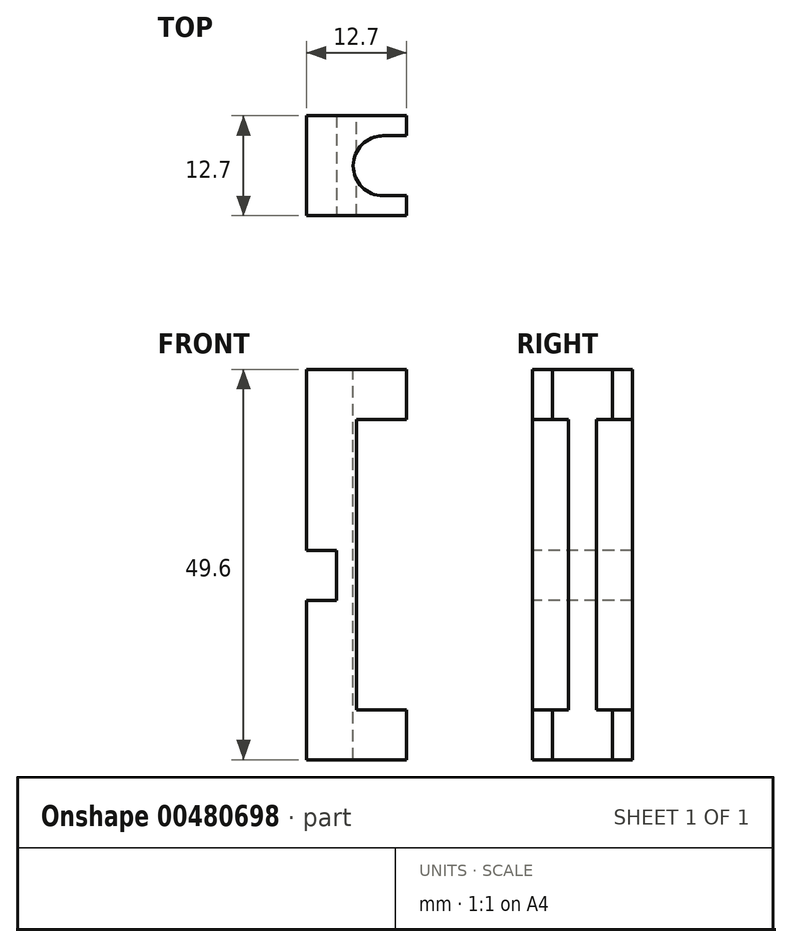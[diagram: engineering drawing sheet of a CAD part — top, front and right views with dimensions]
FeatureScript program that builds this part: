
annotation { "Feature Type Name" : "Feature", "Feature Type Description" : "" }
export const myFeature = defineFeature(function(context is Context, id is Id, definition is map)
    precondition{}
    {
        {
            var Q0;
            Q0=qCreatedBy(makeId("Front.planeOp"),FACE);
            var sketch = newSketch(context, id + "F0", { "sketchPlane" : qUnion([Q0])});
            skLineSegment(sketch, "E0.bottom", {"start": v(-21.97, -16.87) * mm, "end": v(-15.62, -16.87) * mm});
            skLineSegment(sketch, "E0.top", {"start": v(-21.97, 32.73) * mm, "end": v(-15.62, 32.73) * mm});
            skLineSegment(sketch, "E0.left", {"start": v(-21.97, -16.87) * mm, "end": v(-21.97, 32.73) * mm});
            skLineSegment(sketch, "E0.right", {"start": v(-15.62, -16.87) * mm, "end": v(-15.62, 32.73) * mm});
            skLineSegment(sketch, "E1", {"start": v(-15.62, 26.38) * mm, "end": v(-9.27, 26.38) * mm});
            skLineSegment(sketch, "E2", {"start": v(-9.27, 26.38) * mm, "end": v(-9.27, 32.73) * mm});
            skLineSegment(sketch, "E3", {"start": v(-9.27, 32.73) * mm, "end": v(-15.62, 32.73) * mm});
            skLineSegment(sketch, "E4", {"start": v(-15.62, -16.87) * mm, "end": v(-9.27, -16.87) * mm});
            skLineSegment(sketch, "E5", {"start": v(-9.27, -16.87) * mm, "end": v(-9.27, -10.52) * mm});
            skLineSegment(sketch, "E6", {"start": v(-9.27, -10.52) * mm, "end": v(-15.62, -10.52) * mm});
            skSolve(sketch);
        }
        {
            var Q0;
            Q0 = qSketchRegion(id + "F0", true);
            extrude(context, id + "F1", {"entities" : qUnion([Q0]), "depth" : 12.7 * mm, "offsetDistance" : 25.4 * mm});
        }
        {
            var Q0;
            Q0=makeQuery(id+"F1.opExtrude","SWEPT_FACE",FACE,{"disambiguationData":[OSD([sQuery(id+"F0.wireOp",EDGE,"E0.top"),sQuery(id+"F0.wireOp",EDGE,"E3")])]});
            var sketch = newSketch(context, id + "F2", { "sketchPlane" : qUnion([Q0])});
            skLineSegment(sketch, "E7.bottom", {"start": v(-9.27, -10.16) * mm, "end": v(-12.23, -10.16) * mm});
            skLineSegment(sketch, "E7.top", {"start": v(-9.27, -2.54) * mm, "end": v(-12.23, -2.54) * mm});
            skLineSegment(sketch, "E7.left", {"start": v(-9.27, -2.54) * mm, "end": v(-9.27, -10.16) * mm});
            skArc(sketch, "E8", {"start": v(-12.23, -10.16) * mm, "mid": v(-16.04, -6.35) * mm, "end": v(-12.23, -2.54) * mm});
            skSolve(sketch);
        }
        {
            var Q0;
            Q0 = qSketchRegion(id + "F2", true);
            extrude(context, id + "F3", {"entities" : qUnion([Q0]), "operationType" : NewBodyOperationType.REMOVE, "endBound" : BoundingType.THROUGH_ALL, "oppositeDirection" : true, "depth" : 25.4 * mm, "offsetDistance" : 25.4 * mm});
        }
        {
            var Q0;
            Q0=makeQuery(id+"F1.opExtrude","CAP_FACE",FACE,{"disambiguationData":[OSD([sQuery(id+"F0.wireOp",EDGE,"E0.bottom"),sQuery(id+"F0.wireOp",EDGE,"E0.top"),sQuery(id+"F0.wireOp",EDGE,"E0.left"),sQuery(id+"F0.wireOp",EDGE,"E0.right"),sQuery(id+"F0.wireOp",EDGE,"E1"),sQuery(id+"F0.wireOp",EDGE,"E2"),sQuery(id+"F0.wireOp",EDGE,"E3"),sQuery(id+"F0.wireOp",EDGE,"E4"),sQuery(id+"F0.wireOp",EDGE,"E5"),sQuery(id+"F0.wireOp",EDGE,"E6")])],"isStart":false});
            var sketch = newSketch(context, id + "F4", { "sketchPlane" : qUnion([Q0])});
            skLineSegment(sketch, "E9", {"start": v(-21.97, 9.7) * mm, "end": v(-18.16, 9.7) * mm});
            skLineSegment(sketch, "E10", {"start": v(-18.16, 9.7) * mm, "end": v(-18.16, 3.36) * mm});
            skLineSegment(sketch, "E11", {"start": v(-18.16, 3.36) * mm, "end": v(-21.97, 3.36) * mm});
            skLineSegment(sketch, "E12", {"start": v(-21.97, 3.36) * mm, "end": v(-21.97, 9.7) * mm});
            skSolve(sketch);
        }
        {
            var Q0;
            Q0 = qSketchRegion(id + "F4", true);
            extrude(context, id + "F5", {"entities" : qUnion([Q0]), "operationType" : NewBodyOperationType.REMOVE, "oppositeDirection" : true, "depth" : 25.4 * mm, "offsetDistance" : 25.4 * mm});
        }
    });
